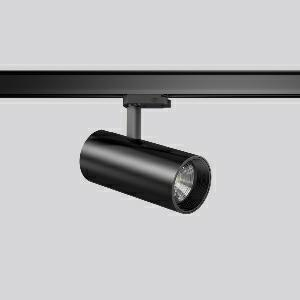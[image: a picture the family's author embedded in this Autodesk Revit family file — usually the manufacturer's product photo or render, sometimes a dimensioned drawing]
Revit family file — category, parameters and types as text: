
# Revit family: deecos_s_mini_742198_003_2_5766
name_source: partatom
category: Lighting Fixtures
units: mm (PartAtom-declared; Revit-internal decimal feet)

## family parameters
Cut with Voids When Loaded = No
Host = Face
Light Source = No
Part Type = Normal
Room Calculation Point = No
Round Connector Dimension = Use Diameter
Shared = No

## types (1)
- DEECOS S mini (1 x LED Modul 927, 2100 lm, 2700)
    Apparent Load = 20 VA
    Approval mark = CE
    CIE Flux Codes = 99 100 100 100 100
    Color Rendering = 92
    Color Temperature = 2700
    Default Elevation = 1800 mm
    Description = Series: DEECOS S mini
LED surface-mounted projector in modern design with no visible cooling ribs. Housing: die-cast aluminium, powder-coated. Rotation range: 356°. Swivel range: 90°. Black plastic ring and recessed LED to prevent glare from the side. Optical assembly with lens made of plastic (polycarbonate) for the best homogeneous light distribution - can be changed without tools. Best colour rendering index Ra>90. With multi adaptor for 3-circuit tracks 230 V. Suitable for Track on ceiling, Wall track. High quality converter without flickering and stroboscopic effect. The following accessories can be mounted without use of tools: interchangeable lenses, decorative glasses, honeycomb louvre, clear and frosted diffusers, white interchangeable plastic ring. 
Colour: deep black, matt (RAL 9005)
Diameter: 87 mm
Height: 214 mm
Lamp: LED
Socket: without socket
Colour temperature: 2700K
Colour rendering index (CRI): 92
System power: 20 W
Rated luminous flux: 2100 lm
Luminous efficiency: 105 lm/W
Control gear: Regulated power supply
Protection class: I
Type of protection: IP 20
    Height = 214 mm
    Lamp = 1 x LED Modul 927
    Lamp Light Flux = 2100 lm
    Lamp count = 1
    Length = 87 mm
    Lifetime = 50000 h
    Luminous efficacy = 105 lm/W
    Manufacturer = RZB
    ModVariant = No
    Model = 742198.003.2
    Mounting Place = Ceiling
    Mounting Type = Rail mounted
    Number of Poles = 1
    OnlyDefault = Yes
    Power Factor = 1
    Product Name = DEECOS S mini
    Product group = Track mounted projectors
    ProductGroupID = 301
    Protection Class = Protection class I
    Protection Degree = IP 20
    RLX_Detail_Level = 1
    RLX_Emergency_Light_Flux = 0 lm
    RLX_Emergency_Type = 0
    RLX_Emergency_Type_DB = No
    RlxData = <blob elided: 38733 chars, md5=aae4a615>
    Socket = socket
    Standby Power = 0 W
    System Light Flux = 2100 lm
    System Power = 20 W
    Type Comments = Product without accessories
    Type Image = 741930.003.jpg
    URL = http://relux.com
    VarID = ---
    Voltage = 230 V
    Voltage Range = 220-240 V
    Weight = 0.00 kg
    Width = 0 mm  [stored 0 ft]

note: [stored X ft] marks values corroborated as IEEE doubles in the binary element streams (Revit-internal decimal feet)

## geometry (parser evidence)
native form markers: Blend x4, Sweep x12
no freeform markers — native parametric forms only
